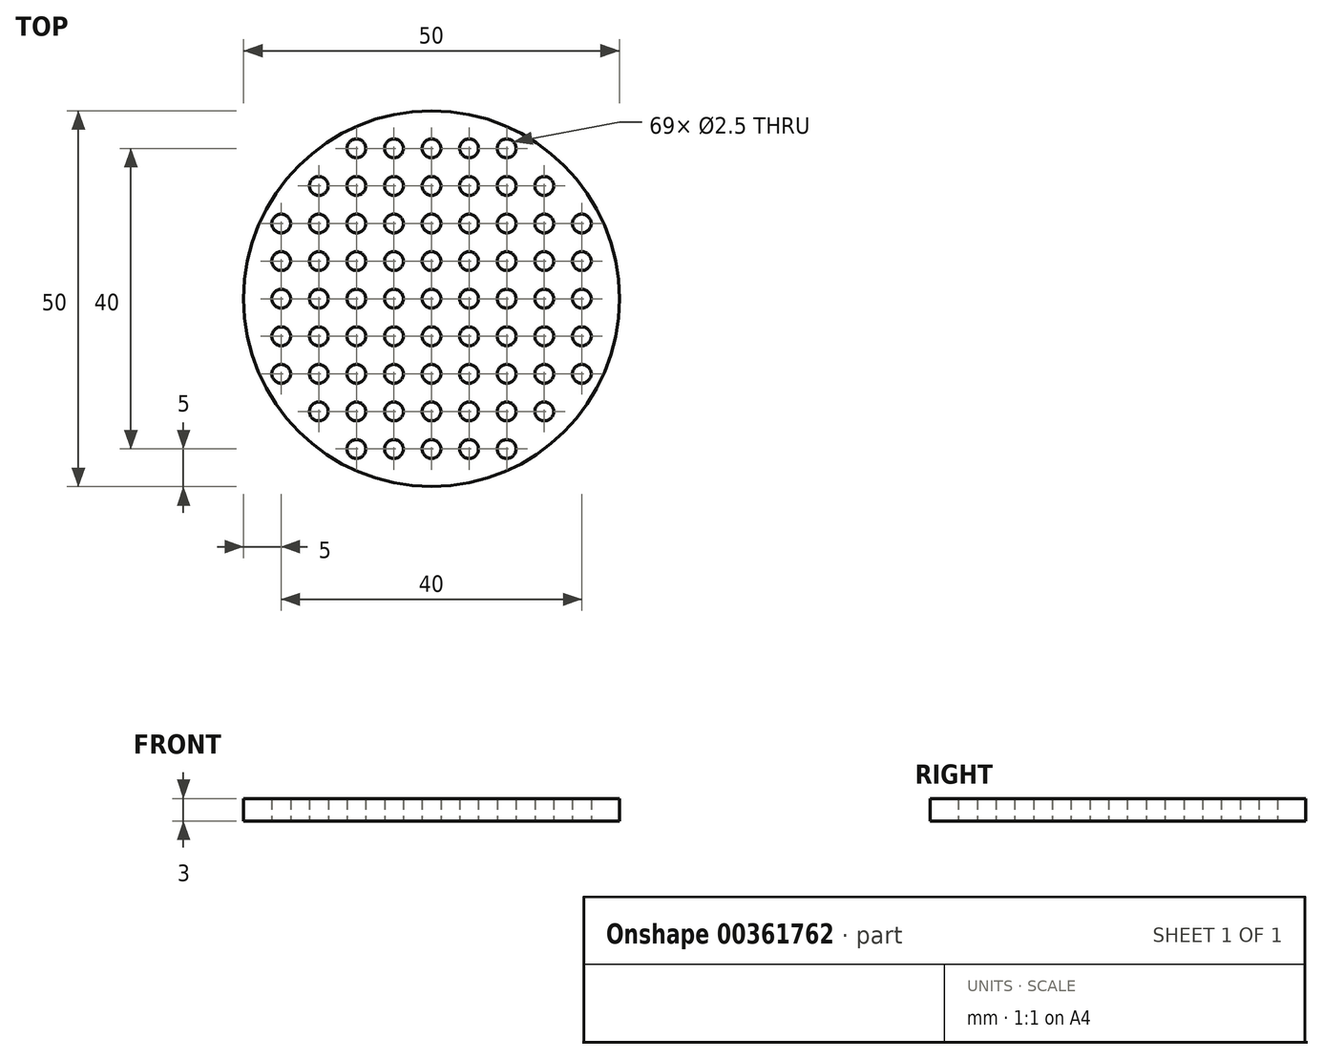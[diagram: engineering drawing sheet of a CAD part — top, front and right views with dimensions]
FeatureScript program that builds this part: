
annotation { "Feature Type Name" : "Feature", "Feature Type Description" : "" }
export const myFeature = defineFeature(function(context is Context, id is Id, definition is map)
    precondition{}
    {
        {
            var Q0;
            Q0=qCreatedBy(makeId("Top.planeOp"),FACE);
            var sketch = newSketch(context, id + "F0", { "sketchPlane" : qUnion([Q0])});
            skCircle(sketch, "E0", {"center": v(0, 0) * mm, "radius": 25 * mm});
            skCircle(sketch, "E1.1.0.0", {"center": v(-20, 0) * mm, "radius": 1.25 * mm});
            skCircle(sketch, "E1.2.0.0", {"center": v(-15, 0) * mm, "radius": 1.25 * mm});
            skCircle(sketch, "E1.3.0.0", {"center": v(-10, 0) * mm, "radius": 1.25 * mm});
            skCircle(sketch, "E1.4.0.0", {"center": v(-5, 0) * mm, "radius": 1.25 * mm});
            skCircle(sketch, "E1.5.0.0", {"center": v(0, 0) * mm, "radius": 1.25 * mm});
            skCircle(sketch, "E1.6.0.0", {"center": v(5, 0) * mm, "radius": 1.25 * mm});
            skCircle(sketch, "E1.7.0.0", {"center": v(10, 0) * mm, "radius": 1.25 * mm});
            skCircle(sketch, "E1.8.0.0", {"center": v(15, 0) * mm, "radius": 1.25 * mm});
            skCircle(sketch, "E1.9.0.0", {"center": v(20, 0) * mm, "radius": 1.25 * mm});
            skCircle(sketch, "E2.0.1.0", {"center": v(-10, 5) * mm, "radius": 1.25 * mm});
            skCircle(sketch, "E2.0.1.1", {"center": v(-15, 5) * mm, "radius": 1.25 * mm});
            skCircle(sketch, "E2.0.1.2", {"center": v(-5, 5) * mm, "radius": 1.25 * mm});
            skCircle(sketch, "E2.0.1.3", {"center": v(5, 5) * mm, "radius": 1.25 * mm});
            skCircle(sketch, "E2.0.1.4", {"center": v(10, 5) * mm, "radius": 1.25 * mm});
            skCircle(sketch, "E2.0.1.5", {"center": v(15, 5) * mm, "radius": 1.25 * mm});
            skCircle(sketch, "E2.0.1.6", {"center": v(20, 5) * mm, "radius": 1.25 * mm});
            skCircle(sketch, "E2.0.1.9", {"center": v(-20, 5) * mm, "radius": 1.25 * mm});
            skCircle(sketch, "E2.0.1.10", {"center": v(0, 5) * mm, "radius": 1.25 * mm});
            skCircle(sketch, "E2.0.2.0", {"center": v(-10, 10) * mm, "radius": 1.25 * mm});
            skCircle(sketch, "E2.0.2.1", {"center": v(-15, 10) * mm, "radius": 1.25 * mm});
            skCircle(sketch, "E2.0.2.2", {"center": v(-5, 10) * mm, "radius": 1.25 * mm});
            skCircle(sketch, "E2.0.2.3", {"center": v(5, 10) * mm, "radius": 1.25 * mm});
            skCircle(sketch, "E2.0.2.4", {"center": v(10, 10) * mm, "radius": 1.25 * mm});
            skCircle(sketch, "E2.0.2.5", {"center": v(15, 10) * mm, "radius": 1.25 * mm});
            skCircle(sketch, "E2.0.2.6", {"center": v(20, 10) * mm, "radius": 1.25 * mm});
            skCircle(sketch, "E2.0.2.9", {"center": v(-20, 10) * mm, "radius": 1.25 * mm});
            skCircle(sketch, "E2.0.2.10", {"center": v(0, 10) * mm, "radius": 1.25 * mm});
            skCircle(sketch, "E2.0.3.0", {"center": v(-10, 15) * mm, "radius": 1.25 * mm});
            skCircle(sketch, "E2.0.3.1", {"center": v(-15, 15) * mm, "radius": 1.25 * mm});
            skCircle(sketch, "E2.0.3.2", {"center": v(-5, 15) * mm, "radius": 1.25 * mm});
            skCircle(sketch, "E2.0.3.3", {"center": v(5, 15) * mm, "radius": 1.25 * mm});
            skCircle(sketch, "E2.0.3.4", {"center": v(10, 15) * mm, "radius": 1.25 * mm});
            skCircle(sketch, "E2.0.3.5", {"center": v(15, 15) * mm, "radius": 1.25 * mm});
            skCircle(sketch, "E2.0.3.10", {"center": v(0, 15) * mm, "radius": 1.25 * mm});
            skCircle(sketch, "E2.0.4.0", {"center": v(-10, 20) * mm, "radius": 1.25 * mm});
            skCircle(sketch, "E2.0.4.2", {"center": v(-5, 20) * mm, "radius": 1.25 * mm});
            skCircle(sketch, "E2.0.4.3", {"center": v(5, 20) * mm, "radius": 1.25 * mm});
            skCircle(sketch, "E2.0.4.4", {"center": v(10, 20) * mm, "radius": 1.25 * mm});
            skCircle(sketch, "E2.0.4.10", {"center": v(0, 20) * mm, "radius": 1.25 * mm});
            skLineSegment(sketch, "E2.direction1", {"start": v(-25, 0) * mm, "end": v(0, 0) * mm, "construction": true});
            skCircle(sketch, "E3.0.1.0", {"center": v(-15, -5) * mm, "radius": 1.25 * mm});
            skCircle(sketch, "E3.0.1.1", {"center": v(-20, -5) * mm, "radius": 1.25 * mm});
            skCircle(sketch, "E3.0.1.2", {"center": v(20, -5) * mm, "radius": 1.25 * mm});
            skCircle(sketch, "E3.0.1.3", {"center": v(15, -5) * mm, "radius": 1.25 * mm});
            skCircle(sketch, "E3.0.1.4", {"center": v(10, -5) * mm, "radius": 1.25 * mm});
            skCircle(sketch, "E3.0.1.5", {"center": v(5, -5) * mm, "radius": 1.25 * mm});
            skCircle(sketch, "E3.0.1.6", {"center": v(0, -5) * mm, "radius": 1.25 * mm});
            skCircle(sketch, "E3.0.1.7", {"center": v(-5, -5) * mm, "radius": 1.25 * mm});
            skCircle(sketch, "E3.0.1.8", {"center": v(-10, -5) * mm, "radius": 1.25 * mm});
            skCircle(sketch, "E3.0.2.0", {"center": v(-15, -10) * mm, "radius": 1.25 * mm});
            skCircle(sketch, "E3.0.2.1", {"center": v(-20, -10) * mm, "radius": 1.25 * mm});
            skCircle(sketch, "E3.0.2.2", {"center": v(20, -10) * mm, "radius": 1.25 * mm});
            skCircle(sketch, "E3.0.2.3", {"center": v(15, -10) * mm, "radius": 1.25 * mm});
            skCircle(sketch, "E3.0.2.4", {"center": v(10, -10) * mm, "radius": 1.25 * mm});
            skCircle(sketch, "E3.0.2.5", {"center": v(5, -10) * mm, "radius": 1.25 * mm});
            skCircle(sketch, "E3.0.2.6", {"center": v(0, -10) * mm, "radius": 1.25 * mm});
            skCircle(sketch, "E3.0.2.7", {"center": v(-5, -10) * mm, "radius": 1.25 * mm});
            skCircle(sketch, "E3.0.2.8", {"center": v(-10, -10) * mm, "radius": 1.25 * mm});
            skCircle(sketch, "E3.0.3.0", {"center": v(-15, -15) * mm, "radius": 1.25 * mm});
            skCircle(sketch, "E3.0.3.3", {"center": v(15, -15) * mm, "radius": 1.25 * mm});
            skCircle(sketch, "E3.0.3.4", {"center": v(10, -15) * mm, "radius": 1.25 * mm});
            skCircle(sketch, "E3.0.3.5", {"center": v(5, -15) * mm, "radius": 1.25 * mm});
            skCircle(sketch, "E3.0.3.6", {"center": v(0, -15) * mm, "radius": 1.25 * mm});
            skCircle(sketch, "E3.0.3.7", {"center": v(-5, -15) * mm, "radius": 1.25 * mm});
            skCircle(sketch, "E3.0.3.8", {"center": v(-10, -15) * mm, "radius": 1.25 * mm});
            skCircle(sketch, "E3.0.4.4", {"center": v(10, -20) * mm, "radius": 1.25 * mm});
            skCircle(sketch, "E3.0.4.5", {"center": v(5, -20) * mm, "radius": 1.25 * mm});
            skCircle(sketch, "E3.0.4.6", {"center": v(0, -20) * mm, "radius": 1.25 * mm});
            skCircle(sketch, "E3.0.4.7", {"center": v(-5, -20) * mm, "radius": 1.25 * mm});
            skCircle(sketch, "E3.0.4.8", {"center": v(-10, -20) * mm, "radius": 1.25 * mm});
            skLineSegment(sketch, "E3.direction1", {"start": v(-20, 0) * mm, "end": v(5, 0) * mm, "construction": true});
            skLineSegment(sketch, "E3.direction2", {"start": v(-20, 0) * mm, "end": v(-20, -5) * mm, "construction": true});
            skSolve(sketch);
        }
        {
            var Q0;
            Q0=makeQuery(id+"F0.imprint","IMPRINT",FACE,{"disambiguationData":[TD([[makeQuery(id+"F0.imprint","IMPRINT",EDGE,{"derivedFrom":sQuery(id+"F0.wireOp",EDGE,"E0")}),1.0]])]});
            extrude(context, id + "F1", {"entities" : qUnion([Q0]), "depth" : 3 * mm});
        }
    });
